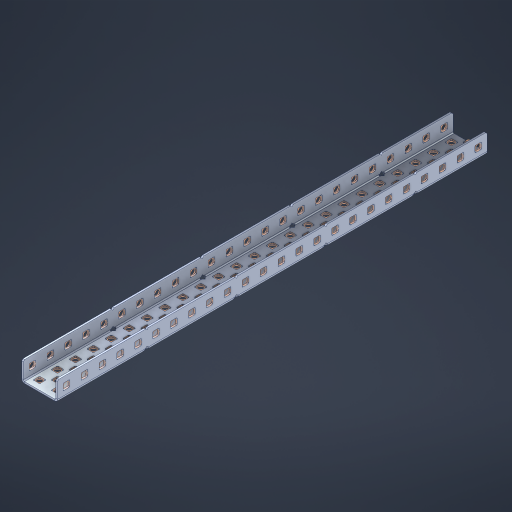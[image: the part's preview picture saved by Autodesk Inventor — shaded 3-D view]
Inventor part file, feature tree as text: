
AUTODESK INVENTOR PART (.ipt)
format: ipt  version: 2023 (Build 270158000, 158)  size: 1,589,760 bytes
history: native  units: in
note: dims shown in document units (in); Inventor stores cm internally (conversion verified against a paired STEP export)
features: other x127, extrude x118, sheet_metal_op x11, sketch x10, pattern_linear x2, mirror x1, chamfer x1
ambient origin geometry x8: Origin, YZ Plane, XZ Plane, XY Plane, X Axis, Y Axis, Z Axis, Center Point
bodies: Solid1 (feature_tree), Body (feature_tree)
feature tree (270):
  sheet_metal_op  "Flanges"
  other  "Flange Pattern Plane"
  other  "Flange Pattern Sketch"
  sheet_metal_op  "Flange Pattern"
  sheet_metal_op  "Body Pattern"
  pattern_linear  "Center Pattern"  Spacing1=0.0469in  [1 undecoded]
  other  "Arc Length"
  mirror  "Notch Mirror"
  pattern_linear  "Notch Pattern"  Spacing1=0.182in  [1 undecoded]
  chamfer  "End Chamfer"
  extrude  "Half Cut"  Depth=0.02in
  sketch  "Sketch1"  dims[d0=1.0in]
  other  "Plate1"
  sketch  "Sketch2"  dims[d1=12.0in]
  other  "Plate2"
  sheet_metal_op  "Bend1"
  sheet_metal_op  "Corner1"
  sketch  "Sketch3"  dims[d2=0.0469in]
  sketch  "Sketch7"  dims[d3=0.0469in]
  other  "Srf1"
  other  "Srf2"
  sketch  "Sketch8"  dims[d4=0.0234in]
  sketch  "Sketch9"  dims[d5=0.0938in]
  other  "Srf91"
  sheet_metal_op  "Body Pattern Sketch"
  other  "Srf92"
  sketch  "Sketch13"  dims[d6=0.0469in]
  sketch  "Sketch14"  dims[d7=0.5in d8=90.0deg d9=0.0312in]
  sketch  "Sketch15"  dims[d10=0.1875in]
  sketch  "Sketch16"  dims[d11=0.0469in d12=0.0469in d16=0.182in d17=0.02in d18=0.0469in d19=0.0in d20=0.25in d21=0.25in d38=9.4488in d40=0.5in d41=0.7874in d43=1.0in d46=0.172in d47=1.0in d48=0.0in d49=0.182in d50=0.02in d51=0.25in d52=0.25in d53=0.0469in d54=0.0in d55=0.172in d56=1.0in d57=0.0in d58=0.25in d60=9.4488in d62=0.5in d63=0.7874in d65=0.5in d85=0.1227in d86=0.1659in d88=0.04in d89=0.0469in d90=0.0in d91=0.04in d92=0.0491in d95=2.5in d96=0.04in d97=0.25in d98=45.0deg d99=0.25in d100=0.5in d101=0.0in d102=2.497in d106=0.182in d107=0.02in d108=0.5in d109=0.5in d110=0.0469in d111=0.0in d112=0.172in d113=0.5in d114=0.0in d117=0.5in d118=0.5in d119=0.5in]
  other  "Srf786"
  other  "Srf823"
  other  "Srf824"
  other  "Srf825"
  other  "Srf826"
  other  "Srf827"
  other  "Srf828"
  other  "Srf829"
  other  "Srf856"
  other  "Srf857"
  other  "Srf858"
  other  "Srf859"
  other  "Srf860"
  other  "Srf861"
  other  "Srf862"
  other  "Srf889"
  other  "Srf890"
  other  "Srf891"
  other  "Srf892"
  other  "Srf893"
  other  "Srf894"
  other  "Srf895"
  other  "Srf896"
  other  "Srf922"
  other  "Srf923"
  other  "Srf924"
  other  "Srf925"
  other  "Srf926"
  other  "Srf959"
  other  "Srf960"
  other  "Srf961"
  other  "Srf962"
  other  "Srf963"
  other  "Srf996"
  other  "Srf997"
  other  "Srf998"
  other  "Srf999"
  other  "Srf1000"
  other  "Srf1143"
  other  "Srf1144"
  other  "Srf1145"
  other  "Srf1146"
  other  "Srf1147"
  other  "Srf1148"
  other  "Srf1149"
  other  "Srf1150"
  other  "Srf1151"
  other  "Srf1152"
  other  "Srf1153"
  other  "Srf1154"
  other  "Srf1155"
  other  "Srf1156"
  other  "Srf1157"
  other  "Srf1158"
  other  "Srf1159"
  other  "Srf1160"
  other  "Srf1161"
  other  "Srf1162"
  other  "Srf1163"
  other  "Srf1164"
  other  "Srf1165"
  other  "Srf1166"
  other  "Srf1167"
  other  "Srf1168"
  other  "Srf1169"
  other  "Srf1170"
  other  "Srf1171"
  other  "Srf1172"
  other  "Srf1173"
  other  "Srf1174"
  other  "Srf1175"
  other  "Srf1176"
  other  "Srf1199"
  other  "Srf1200"
  other  "Srf1201"
  other  "Srf1202"
  other  "Srf1203"
  other  "Srf1204"
  other  "Srf1205"
  other  "Srf1206"
  other  "Srf1207"
  other  "Srf1208"
  other  "Srf1209"
  other  "Srf1210"
  other  "Srf1211"
  other  "Srf1212"
  other  "Srf1213"
  other  "Srf1214"
  other  "Srf1215"
  other  "Srf1216"
  other  "Srf1217"
  other  "Srf1218"
  other  "Srf1219"
  other  "Srf1220"
  other  "Srf1221"
  other  "Srf1222"
  other  "Srf1223"
  other  "Srf1224"
  other  "Srf1225"
  other  "Srf1226"
  other  "Srf1227"
  other  "Srf1228"
  other  "Srf1229"
  other  "Srf1230"
  other  "Srf1231"
  other  "Srf1232"
  other  "Srf1255"
  other  "Srf1256"
  other  "Srf1257"
  other  "Srf1258"
  other  "Srf1259"
  other  "Srf1260"
  other  "Srf1261"
  other  "Srf1262"
  other  "Srf1263"
  other  "Srf1264"
  sheet_metal_op  "Flange Stamp"
  sheet_metal_op  "Flange Circle"
  sheet_metal_op  "Body Stamp"
  sheet_metal_op  "Body Circle"
  other  "Center Stamp"
  other  "Center Circle"
  sheet_metal_op  "Notch"
  extrude  "ExtrusionSrf2"  Depth=0.0469in
  extrude  "ExtrusionSrf92"  TaperAngle=0.0deg  [1 undecoded]
  extrude  "ExtrusionSrf823"  Depth=0.5in
  extrude  "ExtrusionSrf824"  Depth=0.5in
  extrude  "ExtrusionSrf825"  Depth=0.5in
  extrude  "ExtrusionSrf826"  Depth=0.5in
  extrude  "ExtrusionSrf827"  Depth=1.0in TaperAngle=0.0deg
  extrude  "ExtrusionSrf828"  Depth=0.5in
  extrude  "ExtrusionSrf829"  Depth=0.02in
  extrude  "ExtrusionSrf856"  Depth=0.5in
  extrude  "ExtrusionSrf857"  Depth=0.5in
  extrude  "ExtrusionSrf858"  Depth=0.0469in
  extrude  "ExtrusionSrf859"  TaperAngle=0.0deg  [1 undecoded]
  extrude  "ExtrusionSrf860"  Depth=0.5in
  extrude  "ExtrusionSrf861"  Depth=1.0in TaperAngle=0.0deg
  extrude  "ExtrusionSrf862"  Depth=0.5in
  extrude  "ExtrusionSrf889"  Depth=0.5in
  extrude  "ExtrusionSrf890"  Depth=0.5in
  extrude  "ExtrusionSrf891"  Depth=0.5in
  extrude  "ExtrusionSrf892"  Depth=0.5in
  extrude  "ExtrusionSrf893"  Depth=0.5in
  extrude  "ExtrusionSrf894"  Depth=0.0469in
  extrude  "ExtrusionSrf895"  TaperAngle=0.0deg  [1 undecoded]
  extrude  "ExtrusionSrf896"  Depth=0.5in
  extrude  "ExtrusionSrf922"  Depth=0.5in
  extrude  "ExtrusionSrf923"  Depth=2.5in
  extrude  "ExtrusionSrf924"  Depth=0.5in TaperAngle=45.0deg
  extrude  "ExtrusionSrf925"  Depth=0.5in
  extrude  "ExtrusionSrf926"  Depth=0.5in TaperAngle=0.0deg
  extrude  "ExtrusionSrf959"  Depth=0.5in
  extrude  "ExtrusionSrf960"  Depth=0.5in
  extrude  "ExtrusionSrf961"  Depth=0.02in
  extrude  "ExtrusionSrf962"  Depth=0.5in
  extrude  "ExtrusionSrf963"  Depth=0.5in
  extrude  "ExtrusionSrf996"  Depth=0.0469in
  extrude  "ExtrusionSrf997"  TaperAngle=0.0deg  [1 undecoded]
  extrude  "ExtrusionSrf998"  Depth=0.5in
  extrude  "ExtrusionSrf999"  Depth=0.5in TaperAngle=0.0deg
  extrude  "ExtrusionSrf1000"  Depth=0.5in
  extrude  "ExtrusionSrf1143"  Depth=0.5in
  extrude  "ExtrusionSrf1144"  Depth=0.5in
  extrude  "ExtrusionSrf1145"  [1 undecoded]
  extrude  "ExtrusionSrf1146"  [1 undecoded]
  extrude  "ExtrusionSrf1147"  [1 undecoded]
  extrude  "ExtrusionSrf1148"  [1 undecoded]
  extrude  "ExtrusionSrf1149"  [1 undecoded]
  extrude  "ExtrusionSrf1150"  [1 undecoded]
  extrude  "ExtrusionSrf1151"  [1 undecoded]
  extrude  "ExtrusionSrf1152"  [1 undecoded]
  extrude  "ExtrusionSrf1153"  [1 undecoded]
  extrude  "ExtrusionSrf1154"  [1 undecoded]
  extrude  "ExtrusionSrf1155"  [1 undecoded]
  extrude  "ExtrusionSrf1156"  [1 undecoded]
  extrude  "ExtrusionSrf1157"  [1 undecoded]
  extrude  "ExtrusionSrf1158"  [1 undecoded]
  extrude  "ExtrusionSrf1159"  [1 undecoded]
  extrude  "ExtrusionSrf1160"  [1 undecoded]
  extrude  "ExtrusionSrf1161"  [1 undecoded]
  extrude  "ExtrusionSrf1162"  [1 undecoded]
  extrude  "ExtrusionSrf1163"  [1 undecoded]
  extrude  "ExtrusionSrf1164"  [1 undecoded]
  extrude  "ExtrusionSrf1165"  [1 undecoded]
  extrude  "ExtrusionSrf1166"  [1 undecoded]
  extrude  "ExtrusionSrf1167"  [1 undecoded]
  extrude  "ExtrusionSrf1168"  [1 undecoded]
  extrude  "ExtrusionSrf1169"  [1 undecoded]
  extrude  "ExtrusionSrf1170"  [1 undecoded]
  extrude  "ExtrusionSrf1171"  [1 undecoded]
  extrude  "ExtrusionSrf1172"  [1 undecoded]
  extrude  "ExtrusionSrf1173"  [1 undecoded]
  extrude  "ExtrusionSrf1174"  [1 undecoded]
  extrude  "ExtrusionSrf1175"  [1 undecoded]
  extrude  "ExtrusionSrf1176"  [1 undecoded]
  extrude  "ExtrusionSrf1199"  [1 undecoded]
  extrude  "ExtrusionSrf1200"  [1 undecoded]
  extrude  "ExtrusionSrf1201"  [1 undecoded]
  extrude  "ExtrusionSrf1202"  [1 undecoded]
  extrude  "ExtrusionSrf1203"  [1 undecoded]
  extrude  "ExtrusionSrf1204"  [1 undecoded]
  extrude  "ExtrusionSrf1205"  [1 undecoded]
  extrude  "ExtrusionSrf1206"  [1 undecoded]
  extrude  "ExtrusionSrf1207"  [1 undecoded]
  extrude  "ExtrusionSrf1208"  [1 undecoded]
  extrude  "ExtrusionSrf1209"  [1 undecoded]
  extrude  "ExtrusionSrf1210"  [1 undecoded]
  extrude  "ExtrusionSrf1211"  [1 undecoded]
  extrude  "ExtrusionSrf1212"  [1 undecoded]
  extrude  "ExtrusionSrf1213"  [1 undecoded]
  extrude  "ExtrusionSrf1214"  [1 undecoded]
  extrude  "ExtrusionSrf1215"  [1 undecoded]
  extrude  "ExtrusionSrf1216"  [1 undecoded]
  extrude  "ExtrusionSrf1217"  [1 undecoded]
  extrude  "ExtrusionSrf1218"  [1 undecoded]
  extrude  "ExtrusionSrf1219"  [1 undecoded]
  extrude  "ExtrusionSrf1220"  [1 undecoded]
  extrude  "ExtrusionSrf1221"  [1 undecoded]
  extrude  "ExtrusionSrf1222"  [1 undecoded]
  extrude  "ExtrusionSrf1223"  [1 undecoded]
  extrude  "ExtrusionSrf1224"  [1 undecoded]
  extrude  "ExtrusionSrf1225"  [1 undecoded]
  extrude  "ExtrusionSrf1226"  [1 undecoded]
  extrude  "ExtrusionSrf1227"  [1 undecoded]
  extrude  "ExtrusionSrf1228"  [1 undecoded]
  extrude  "ExtrusionSrf1229"  [1 undecoded]
  extrude  "ExtrusionSrf1230"  [1 undecoded]
  extrude  "ExtrusionSrf1231"  [1 undecoded]
  extrude  "ExtrusionSrf1232"  [1 undecoded]
  extrude  "ExtrusionSrf1255"  [1 undecoded]
  extrude  "ExtrusionSrf1256"  [1 undecoded]
  extrude  "ExtrusionSrf1257"  [1 undecoded]
  extrude  "ExtrusionSrf1258"  [1 undecoded]
  extrude  "ExtrusionSrf1259"  [1 undecoded]
  extrude  "ExtrusionSrf1260"  [1 undecoded]
  extrude  "ExtrusionSrf1261"  [1 undecoded]
  extrude  "ExtrusionSrf1262"  [1 undecoded]
  extrude  "ExtrusionSrf1263"  [1 undecoded]
  extrude  "ExtrusionSrf1264"  [1 undecoded]
note: 82 required parameter values undecoded (feature->parameter linkage not recoverable at this tier; creation-order binding heuristic only, values carry confidence <= 0.55)
